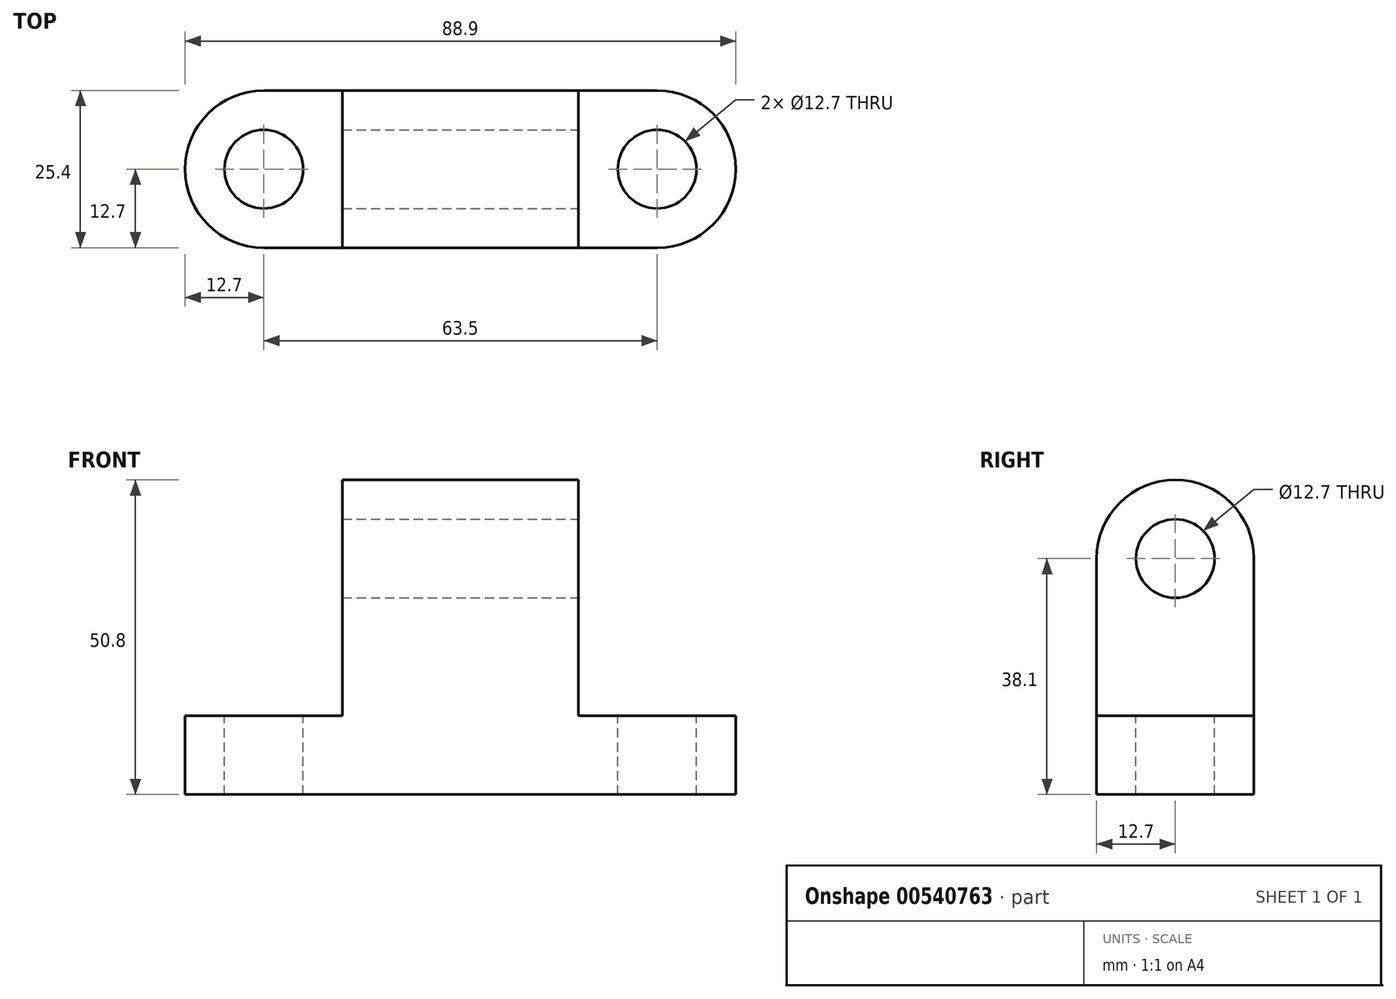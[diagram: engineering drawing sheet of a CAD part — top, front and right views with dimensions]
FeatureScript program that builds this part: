
annotation { "Feature Type Name" : "Feature", "Feature Type Description" : "" }
export const myFeature = defineFeature(function(context is Context, id is Id, definition is map)
    precondition{}
    {
        {
            var Q0;
            Q0=qCreatedBy(makeId("Front.planeOp"),FACE);
            var sketch = newSketch(context, id + "F0", { "sketchPlane" : qUnion([Q0])});
            skLineSegment(sketch, "E0", {"start": v(0, 0) * mm, "end": v(101.6, 0) * mm});
            skLineSegment(sketch, "E1", {"start": v(101.6, 0) * mm, "end": v(101.6, 12.7) * mm});
            skLineSegment(sketch, "E2", {"start": v(101.6, 12.7) * mm, "end": v(69.85, 12.7) * mm});
            skLineSegment(sketch, "E3", {"start": v(69.85, 12.7) * mm, "end": v(69.85, 50.8) * mm});
            skLineSegment(sketch, "E4", {"start": v(69.85, 50.8) * mm, "end": v(31.75, 50.8) * mm});
            skLineSegment(sketch, "E5", {"start": v(31.75, 50.8) * mm, "end": v(31.75, 12.7) * mm});
            skLineSegment(sketch, "E6", {"start": v(31.75, 12.7) * mm, "end": v(0, 12.7) * mm});
            skLineSegment(sketch, "E7", {"start": v(0, 12.7) * mm, "end": v(0, 0) * mm});
            skSolve(sketch);
        }
        {
            var Q0;
            Q0=makeQuery(id+"F0.imprint","IMPRINT",FACE,{"disambiguationData":[TD([[makeQuery(id+"F0.imprint","IMPRINT",EDGE,{"derivedFrom":sQuery(id+"F0.wireOp",EDGE,"E0")}),1.0]])]});
            extrude(context, id + "F1", {"entities" : qUnion([Q0]), "oppositeDirection" : true, "depth" : 25.4 * mm, "offsetDistance" : 25.4 * mm});
        }
        {
            var Q0;
            Q0=makeQuery(id+"F1.opExtrude","SWEPT_FACE",FACE,{"disambiguationData":[OSD([sQuery(id+"F0.wireOp",EDGE,"E2")])]});
            var sketch = newSketch(context, id + "F2", { "sketchPlane" : qUnion([Q0])});
            skCircle(sketch, "E8", {"center": v(82.55, 12.7) * mm, "radius": 6.35 * mm});
            skArc(sketch, "E9", {"start": v(82.55, 0) * mm, "mid": v(95.25, 12.7) * mm, "end": v(82.55, 25.4) * mm});
            skSolve(sketch);
        }
        {
            var Q0;
            Q0=makeQuery(id+"F2.imprint","IMPRINT",FACE,{"disambiguationData":[TD([[makeQuery(id+"F2.imprint","IMPRINT",EDGE,{"derivedFrom":sQuery(id+"F2.wireOp",EDGE,"E8")}),1.0]])]});
            var Q1;
            {var subQ0=sQuery(id+"F2.wireOp",EDGE,"E9");Q1=makeQuery(id+"F2.imprint","IMPRINT",FACE,{"disambiguationData":[TD([[makeQuery(id+"F2.imprint","IMPRINT",EDGE,{"derivedFrom":subQ0}),-1.0]])]});}
            extrude(context, id + "F3", {"entities" : qUnion([Q0, Q1]), "operationType" : NewBodyOperationType.REMOVE, "oppositeDirection" : true, "depth" : 25.4 * mm, "offsetDistance" : 25.4 * mm});
        }
        {
            var Q0;
            Q0=makeQuery(id+"F1.opExtrude","SWEPT_FACE",FACE,{"disambiguationData":[OSD([sQuery(id+"F0.wireOp",EDGE,"E3")])]});
            var sketch = newSketch(context, id + "F4", { "sketchPlane" : qUnion([Q0])});
            skCircle(sketch, "E10", {"center": v(12.7, 38.1) * mm, "radius": 6.35 * mm});
            skArc(sketch, "E11", {"start": v(25.4, 38.1) * mm, "mid": v(12.7, 50.8) * mm, "end": v(0, 38.1) * mm});
            skSolve(sketch);
        }
        {
            var Q0;
            Q0=makeQuery(id+"F4.imprint","IMPRINT",FACE,{"disambiguationData":[TD([[makeQuery(id+"F4.imprint","IMPRINT",EDGE,{"derivedFrom":sQuery(id+"F4.wireOp",EDGE,"E10")}),1.0]])]});
            var Q1;
            {var subQ0=sQuery(id+"F4.wireOp",EDGE,"E11");var subQ1=sQuery(id+"F0.wireOp",EDGE,"E3");var subQ2=makeQuery(id+"F1.opExtrude","CAP_EDGE",EDGE,{"disambiguationData":[OSD([subQ1])],"isStart":false});var subQ3=makeQuery(id+"F4.imprint","INTERSECT",VERTEX,{"derivedFrom":[subQ2,subQ0]});Q1=makeQuery(id+"F4.imprint","IMPRINT",FACE,{"disambiguationData":[TD([[makeQuery(id+"F4.imprint","IMPRINT",EDGE,{"disambiguationData":[TD([[subQ3,-1.0]])],"derivedFrom":subQ0}),-1.0]])]});}
            var Q2;
            {var subQ0=sQuery(id+"F4.wireOp",EDGE,"E11");var subQ1=sQuery(id+"F0.wireOp",EDGE,"E3");var subQ2=makeQuery(id+"F1.opExtrude","CAP_EDGE",EDGE,{"disambiguationData":[OSD([subQ1])],"isStart":true});var subQ3=makeQuery(id+"F4.imprint","INTERSECT",VERTEX,{"derivedFrom":[subQ2,subQ0]});Q2=makeQuery(id+"F4.imprint","IMPRINT",FACE,{"disambiguationData":[TD([[makeQuery(id+"F4.imprint","IMPRINT",EDGE,{"disambiguationData":[TD([[subQ3,1.0]])],"derivedFrom":subQ0}),-1.0]])]});}
            extrude(context, id + "F5", {"entities" : qUnion([Q0, Q1, Q2]), "operationType" : NewBodyOperationType.REMOVE, "oppositeDirection" : true, "depth" : 49.28 * mm, "offsetDistance" : 25.4 * mm});
        }
        {
            var Q0;
            Q0=makeQuery(id+"F1.opExtrude","SWEPT_FACE",FACE,{"disambiguationData":[OSD([sQuery(id+"F0.wireOp",EDGE,"E6")])]});
            var sketch = newSketch(context, id + "F6", { "sketchPlane" : qUnion([Q0])});
            skCircle(sketch, "E12", {"center": v(19.05, 12.7) * mm, "radius": 6.35 * mm});
            skArc(sketch, "E13", {"start": v(19.05, 25.4) * mm, "mid": v(6.35, 12.7) * mm, "end": v(19.05, 0) * mm});
            skPoint(sketch, "E13.startSnap0", {"position": v(15.88, 25.4) * mm});
            skSolve(sketch);
        }
        {
            var Q0;
            {var subQ0=sQuery(id+"F6.wireOp",EDGE,"E13");Q0=makeQuery(id+"F6.imprint","IMPRINT",FACE,{"disambiguationData":[TD([[makeQuery(id+"F6.imprint","IMPRINT",EDGE,{"derivedFrom":subQ0}),-1.0]])]});}
            var Q1;
            Q1=makeQuery(id+"F6.imprint","IMPRINT",FACE,{"disambiguationData":[TD([[makeQuery(id+"F6.imprint","IMPRINT",EDGE,{"derivedFrom":sQuery(id+"F6.wireOp",EDGE,"E12")}),1.0]])]});
            extrude(context, id + "F7", {"entities" : qUnion([Q0, Q1]), "operationType" : NewBodyOperationType.REMOVE, "oppositeDirection" : true, "depth" : 25.4 * mm, "offsetDistance" : 25.4 * mm});
        }
    });
